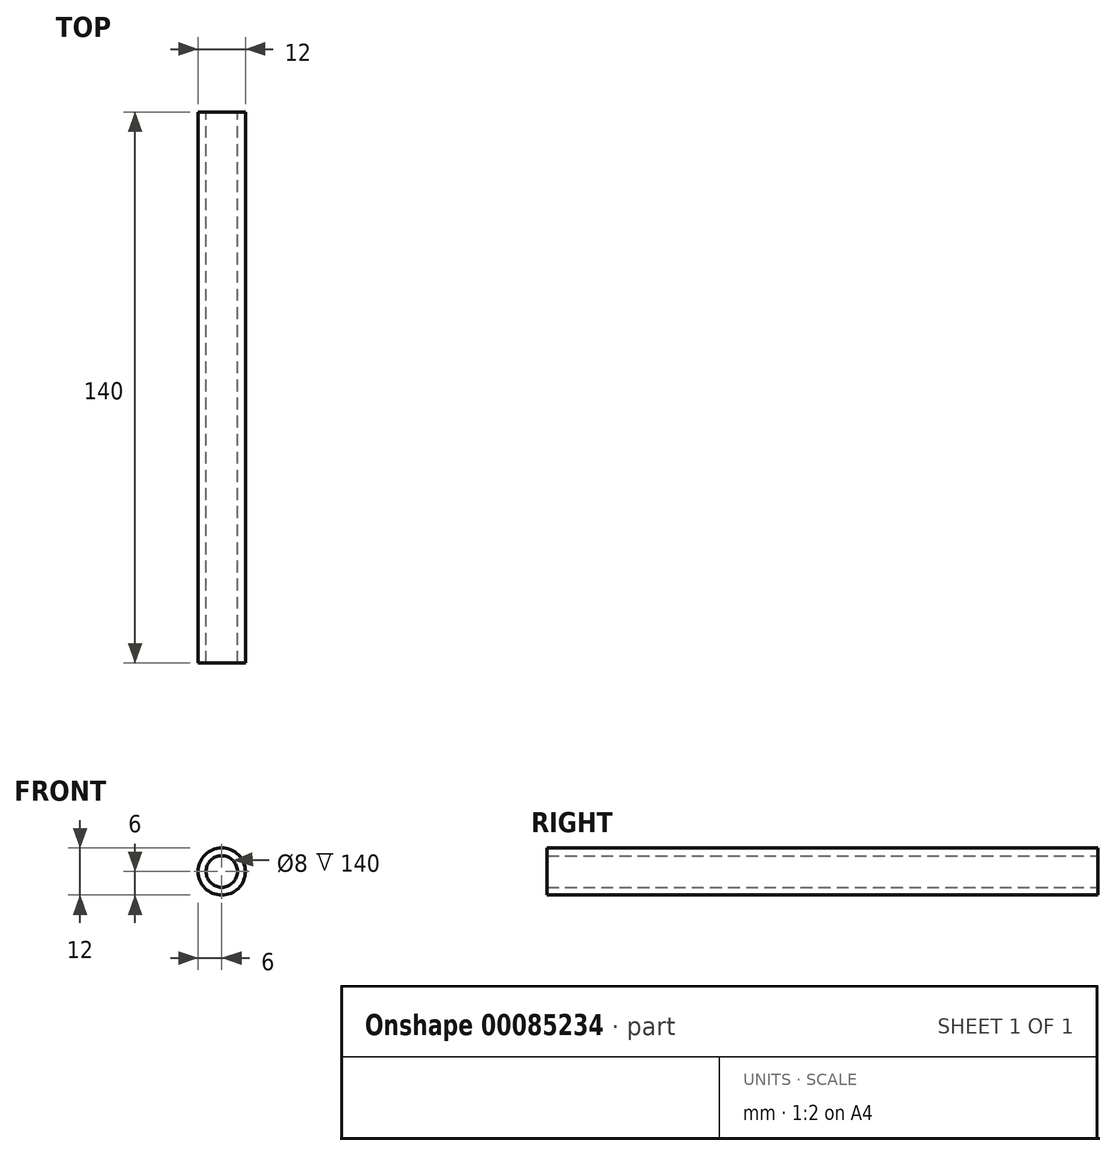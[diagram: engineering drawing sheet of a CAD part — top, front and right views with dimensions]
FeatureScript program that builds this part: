
annotation { "Feature Type Name" : "Feature", "Feature Type Description" : "" }
export const myFeature = defineFeature(function(context is Context, id is Id, definition is map)
    precondition{}
    {
        {
            var Q0;
            Q0=qCreatedBy(makeId("Front.planeOp"),FACE);
            var sketch = newSketch(context, id + "F0", { "sketchPlane" : qUnion([Q0])});
            skCircle(sketch, "E0", {"center": v(0, 0) * mm, "radius": 6 * mm});
            skCircle(sketch, "E1", {"center": v(0, 0) * mm, "radius": 4 * mm});
            skSolve(sketch);
        }
        {
            var Q0;
            Q0 = qSketchRegion(id + "F0", true);
            extrude(context, id + "F1", {"entities" : qUnion([Q0]), "endBound" : BoundingType.SYMMETRIC, "depth" : 140 * mm});
        }
    });
